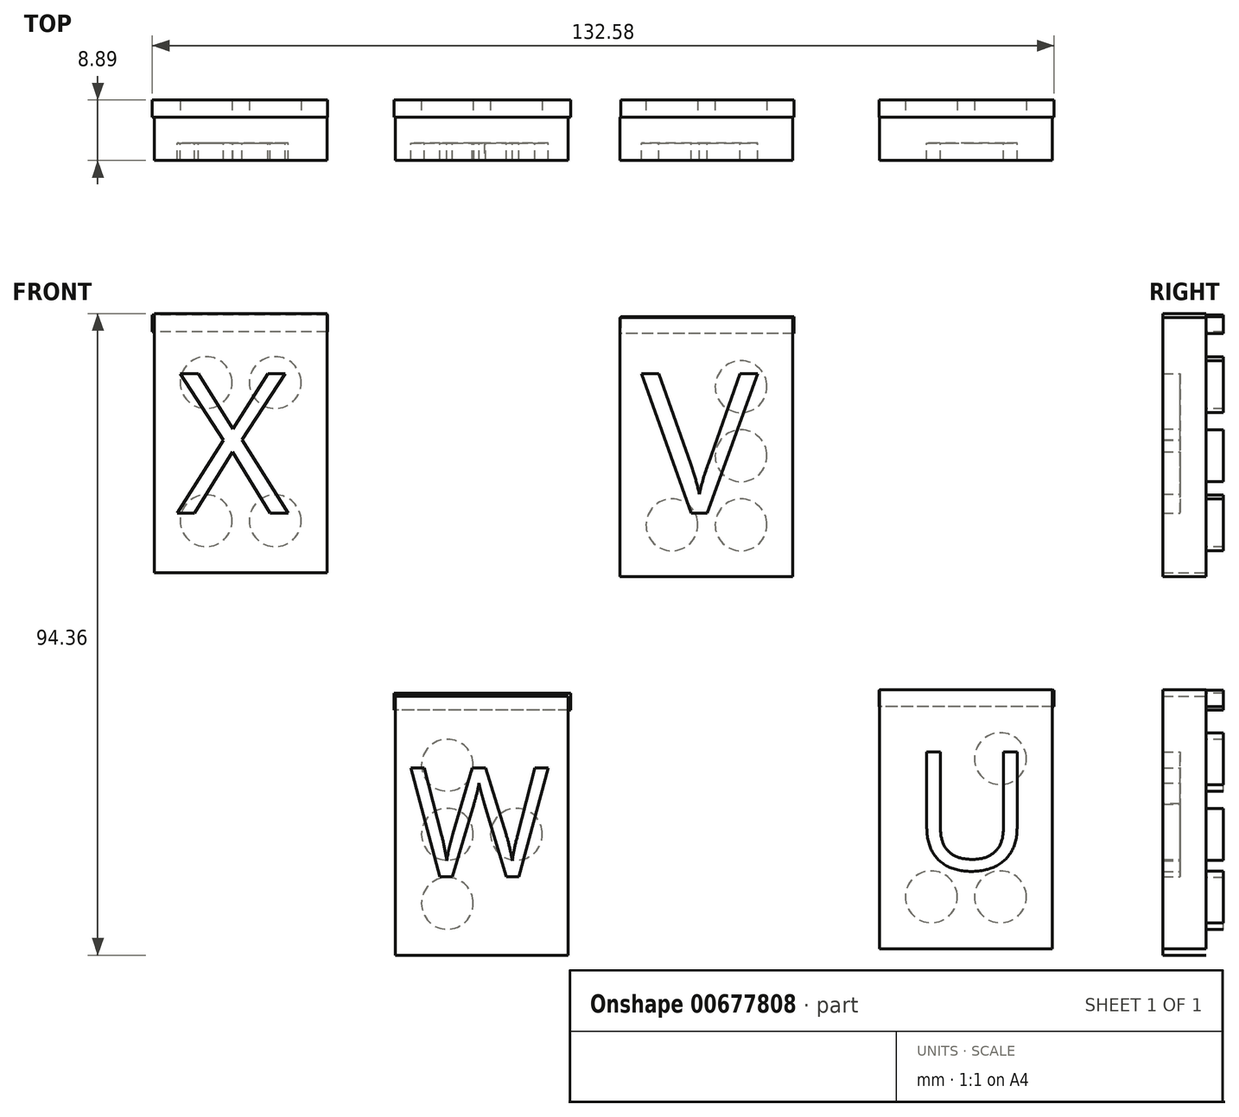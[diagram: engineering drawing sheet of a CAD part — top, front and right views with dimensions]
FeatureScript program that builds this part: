
annotation { "Feature Type Name" : "Feature", "Feature Type Description" : "" }
export const myFeature = defineFeature(function(context is Context, id is Id, definition is map)
    precondition{}
    {
        {
            var Q0;
            Q0=qCreatedBy(makeId("Front.planeOp"),FACE);
            var sketch = newSketch(context, id + "F0", { "sketchPlane" : qUnion([Q0])});
            skLineSegment(sketch, "E0.bottom", {"start": v(-58.76, 38.35) * mm, "end": v(-33.36, 38.35) * mm});
            skLineSegment(sketch, "E0.top", {"start": v(-58.76, 0.25) * mm, "end": v(-33.36, 0.25) * mm});
            skLineSegment(sketch, "E0.left", {"start": v(-58.76, 38.35) * mm, "end": v(-58.76, 0.25) * mm});
            skLineSegment(sketch, "E0.right", {"start": v(-33.36, 38.35) * mm, "end": v(-33.36, 0.25) * mm});
            skLineSegment(sketch, "E1.bottom", {"start": v(-23.3, -17.91) * mm, "end": v(2.1, -17.91) * mm});
            skLineSegment(sketch, "E1.top", {"start": v(-23.3, -56.01) * mm, "end": v(2.1, -56.01) * mm});
            skLineSegment(sketch, "E1.left", {"start": v(-23.3, -17.91) * mm, "end": v(-23.3, -56.01) * mm});
            skLineSegment(sketch, "E1.right", {"start": v(2.1, -17.91) * mm, "end": v(2.1, -56.01) * mm});
            skLineSegment(sketch, "E2.bottom", {"start": v(47.85, -16.96) * mm, "end": v(73.25, -16.96) * mm});
            skLineSegment(sketch, "E2.top", {"start": v(47.85, -55.06) * mm, "end": v(73.25, -55.06) * mm});
            skLineSegment(sketch, "E2.left", {"start": v(47.85, -16.96) * mm, "end": v(47.85, -55.06) * mm});
            skLineSegment(sketch, "E2.right", {"start": v(73.25, -16.96) * mm, "end": v(73.25, -55.06) * mm});
            skLineSegment(sketch, "E3.bottom", {"start": v(9.7, 37.75) * mm, "end": v(35.1, 37.75) * mm});
            skLineSegment(sketch, "E3.top", {"start": v(9.7, -0.35) * mm, "end": v(35.1, -0.35) * mm});
            skLineSegment(sketch, "E3.left", {"start": v(9.7, 37.75) * mm, "end": v(9.7, -0.35) * mm});
            skLineSegment(sketch, "E3.right", {"start": v(35.1, 37.75) * mm, "end": v(35.1, -0.35) * mm});
            skSolve(sketch);
        }
        {
            var Q0;
            Q0=qSketchRegion(id+"F0",true);
            extrude(context, id + "F1", {"entities" : qUnion([Q0]), "depth" : 6.35 * mm});
        }
        {
            var Q0;
            Q0=qCreatedBy(makeId("Front.planeOp"),FACE);
            var sketch = newSketch(context, id + "F2", { "sketchPlane" : qUnion([Q0])});
            skCircle(sketch, "E4", {"center": v(27.49, 7.27) * mm, "radius": 3.81 * mm});
            skCircle(sketch, "E5", {"center": v(27.49, 17.43) * mm, "radius": 3.81 * mm});
            skCircle(sketch, "E6", {"center": v(65.63, -27.12) * mm, "radius": 3.81 * mm});
            skCircle(sketch, "E7", {"center": v(65.63, -47.44) * mm, "radius": 3.81 * mm});
            skCircle(sketch, "E8", {"center": v(-5.52, -38.23) * mm, "radius": 3.81 * mm});
            skCircle(sketch, "E9", {"center": v(-15.68, -28.07) * mm, "radius": 3.81 * mm});
            skCircle(sketch, "E10", {"center": v(27.49, 27.59) * mm, "radius": 3.81 * mm});
            skCircle(sketch, "E11", {"center": v(17.33, 7.27) * mm, "radius": 3.81 * mm});
            skCircle(sketch, "E12", {"center": v(-15.68, -48.4) * mm, "radius": 3.8 * mm});
            skCircle(sketch, "E13", {"center": v(-40.98, 28.19) * mm, "radius": 3.81 * mm});
            skCircle(sketch, "E14", {"center": v(-51.14, 28.19) * mm, "radius": 3.81 * mm});
            skCircle(sketch, "E15", {"center": v(-51.14, 7.87) * mm, "radius": 3.81 * mm});
            skCircle(sketch, "E16", {"center": v(-40.98, 7.87) * mm, "radius": 3.81 * mm});
            skCircle(sketch, "E17", {"center": v(55.47, -47.44) * mm, "radius": 3.81 * mm});
            skCircle(sketch, "E18", {"center": v(-15.68, -38.23) * mm, "radius": 3.81 * mm});
            skSolve(sketch);
        }
        {
            var Q0;
            Q0=qSketchRegion(id+"F2",true);
            extrude(context, id + "F3", {"entities" : qUnion([Q0]), "operationType" : NewBodyOperationType.ADD, "oppositeDirection" : true, "depth" : 2.54 * mm});
        }
        {
            var Q0;
            Q0=qCreatedBy(makeId("Front.planeOp"),FACE);
            cPlane(context, id + "F4", {"entities" : qUnion([Q0]), "cplaneType" : CPlaneType.OFFSET, "offset" : 3.8 * mm, "width" : 152.4 * mm, "height" : 152.4 * mm});
        }
        {
            var Q0;
            Q0=qCreatedBy(id+"F4.planeOp",FACE);
            var sketch = newSketch(context, id + "F5", { "sketchPlane" : qUnion([Q0])});
            skText(sketch, "E19", { "text": "U", "fontName": "OpenSans-Regular.ttf"});
            skText(sketch, "E20", { "text": "V", "fontName": "OpenSans-Regular.ttf"});
            skText(sketch, "E21", { "text": "W", "fontName": "OpenSans-Regular.ttf"});
            skText(sketch, "E22", { "text": "X", "fontName": "OpenSans-Regular.ttf"});
            const initialGuessF5  = {"E19": [0.0526, -0.04345, 1, 0, 0.01749], "E20": [0.01285, 0.009, 1, 0, 0.02066], "E21": [-0.02133, -0.0445, 1, 0, 0.01616], "E22": [-0.0555, 0.009, 1, 0, 0.02066]};
            skSetInitialGuess(sketch, initialGuessF5);
            skSolve(sketch);
        }
        {
            var Q0;
            Q0=qSketchRegion(id+"F5",true);
            extrude(context, id + "F6", {"entities" : qUnion([Q0]), "operationType" : NewBodyOperationType.REMOVE, "depth" : 25.4 * mm});
        }
        {
            var Q0;
            Q0=qCreatedBy(makeId("Front.planeOp"),FACE);
            var sketch = newSketch(context, id + "F7", { "sketchPlane" : qUnion([Q0])});
            skLineSegment(sketch, "E23.bottom", {"start": v(73.52, -17.03) * mm, "end": v(47.79, -17.03) * mm});
            skLineSegment(sketch, "E23.top", {"start": v(73.52, -19.48) * mm, "end": v(47.79, -19.48) * mm});
            skLineSegment(sketch, "E23.left", {"start": v(73.52, -17.03) * mm, "end": v(73.52, -19.48) * mm});
            skLineSegment(sketch, "E23.right", {"start": v(47.79, -17.03) * mm, "end": v(47.79, -19.48) * mm});
            skLineSegment(sketch, "E24.bottom", {"start": v(35.29, 37.86) * mm, "end": v(9.8, 37.86) * mm});
            skLineSegment(sketch, "E24.top", {"start": v(35.29, 35.41) * mm, "end": v(9.8, 35.41) * mm});
            skLineSegment(sketch, "E24.left", {"start": v(35.29, 37.86) * mm, "end": v(35.29, 35.41) * mm});
            skLineSegment(sketch, "E24.right", {"start": v(9.8, 37.86) * mm, "end": v(9.8, 35.41) * mm});
            skLineSegment(sketch, "E25.bottom", {"start": v(-33.33, 38.1) * mm, "end": v(-59.06, 38.1) * mm});
            skLineSegment(sketch, "E25.top", {"start": v(-33.33, 35.66) * mm, "end": v(-59.06, 35.66) * mm});
            skLineSegment(sketch, "E25.left", {"start": v(-33.33, 38.1) * mm, "end": v(-33.33, 35.66) * mm});
            skLineSegment(sketch, "E25.right", {"start": v(-59.06, 38.1) * mm, "end": v(-59.06, 35.66) * mm});
            skLineSegment(sketch, "E26.bottom", {"start": v(2.45, -17.52) * mm, "end": v(-23.53, -17.52) * mm});
            skLineSegment(sketch, "E26.top", {"start": v(2.45, -19.97) * mm, "end": v(-23.53, -19.97) * mm});
            skLineSegment(sketch, "E26.left", {"start": v(2.45, -17.52) * mm, "end": v(2.45, -19.97) * mm});
            skLineSegment(sketch, "E26.right", {"start": v(-23.53, -17.52) * mm, "end": v(-23.53, -19.97) * mm});
            skSolve(sketch);
        }
        {
            var Q0;
            Q0=qSketchRegion(id+"F7",true);
            extrude(context, id + "F8", {"entities" : qUnion([Q0]), "operationType" : NewBodyOperationType.ADD, "oppositeDirection" : true, "depth" : 2.54 * mm});
        }
    });
